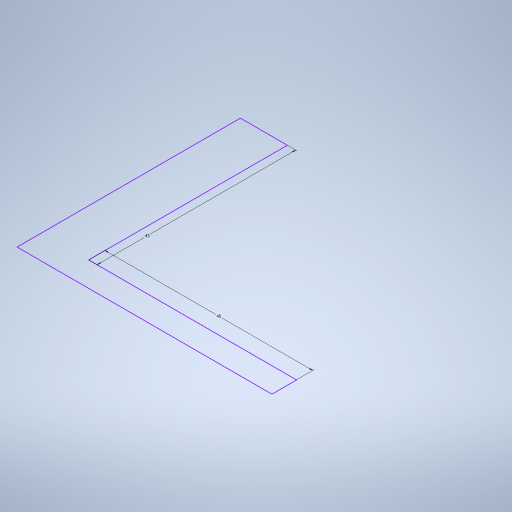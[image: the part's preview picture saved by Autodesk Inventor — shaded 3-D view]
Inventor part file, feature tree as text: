
AUTODESK INVENTOR PART (.ipt)
format: ipt  version: 2024 (Build 280153000, 153)  size: 231,936 bytes
history: native  units: mm
features: sketch x1
ambient origin geometry x8: Origin, YZ Plane, XZ Plane, XY Plane, X Axis, Y Axis, Z Axis, Center Point
feature tree (1):
  sketch  "Sketch1"  dims[d0=43.0mm d1=45.0mm]
